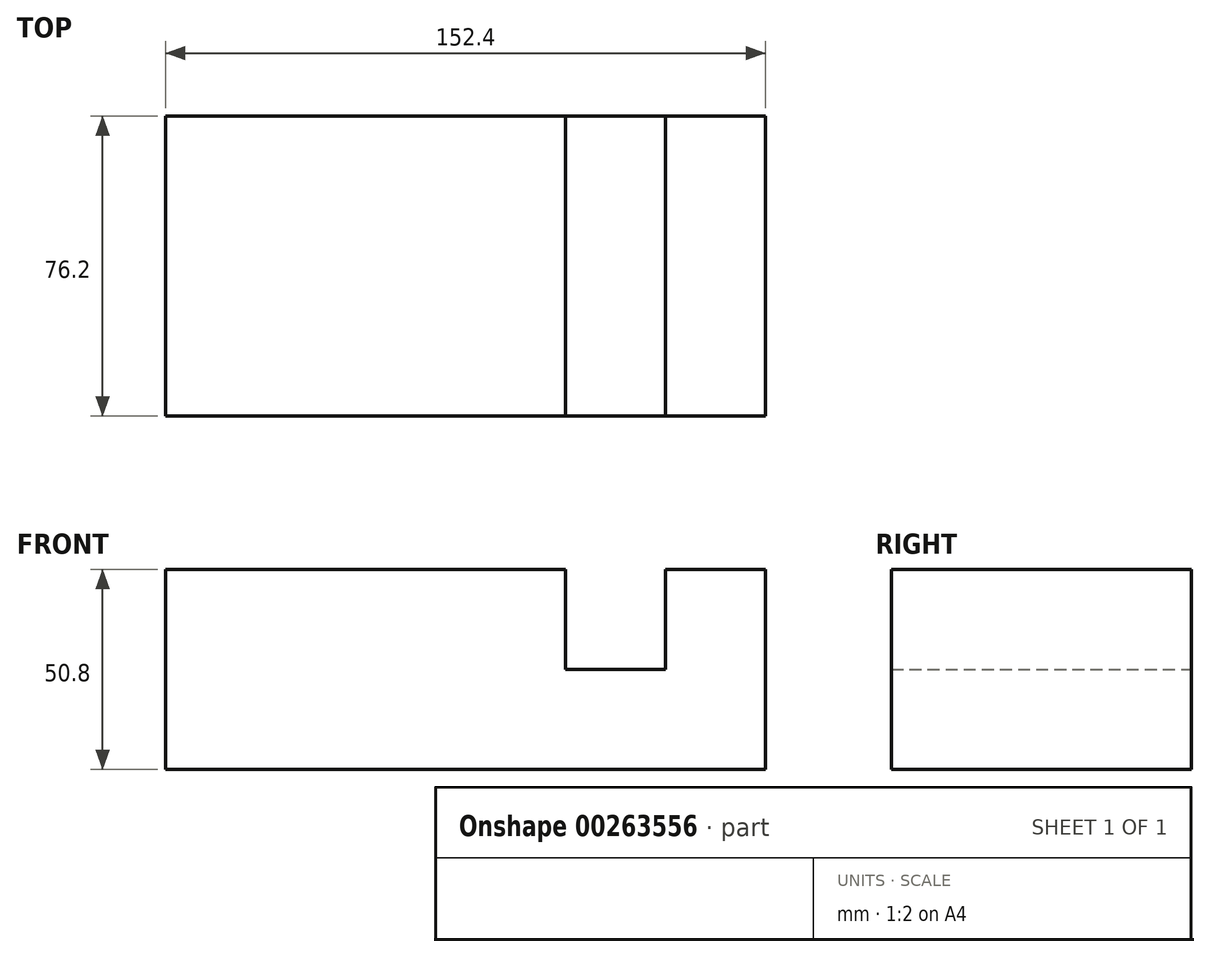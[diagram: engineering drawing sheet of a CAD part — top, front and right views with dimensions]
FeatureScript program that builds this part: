
annotation { "Feature Type Name" : "Feature", "Feature Type Description" : "" }
export const myFeature = defineFeature(function(context is Context, id is Id, definition is map)
    precondition{}
    {
        {
            var Q0;
            Q0=qCreatedBy(makeId("Front.planeOp"),FACE);
            var sketch = newSketch(context, id + "F0", { "sketchPlane" : qUnion([Q0])});
            skLineSegment(sketch, "E0", {"start": v(-57.56, -25.4) * mm, "end": v(94.84, -25.4) * mm});
            skLineSegment(sketch, "E1", {"start": v(94.84, -25.4) * mm, "end": v(94.84, 25.4) * mm});
            skLineSegment(sketch, "E2", {"start": v(94.84, 25.4) * mm, "end": v(69.44, 25.4) * mm});
            skLineSegment(sketch, "E3", {"start": v(69.44, 25.4) * mm, "end": v(69.44, 0) * mm});
            skLineSegment(sketch, "E4", {"start": v(69.44, 0) * mm, "end": v(44.04, 0) * mm});
            skLineSegment(sketch, "E5", {"start": v(44.04, 0) * mm, "end": v(44.04, 25.4) * mm});
            skLineSegment(sketch, "E6", {"start": v(44.04, 25.4) * mm, "end": v(-57.56, 25.4) * mm});
            skLineSegment(sketch, "E7", {"start": v(-57.56, 25.4) * mm, "end": v(-57.56, -25.4) * mm});
            skSolve(sketch);
        }
        {
            var Q0;
            Q0 = qSketchRegion(id + "F0", true);
            extrude(context, id + "F1", {"entities" : qUnion([Q0]), "depth" : 76.2 * mm});
        }
    });
